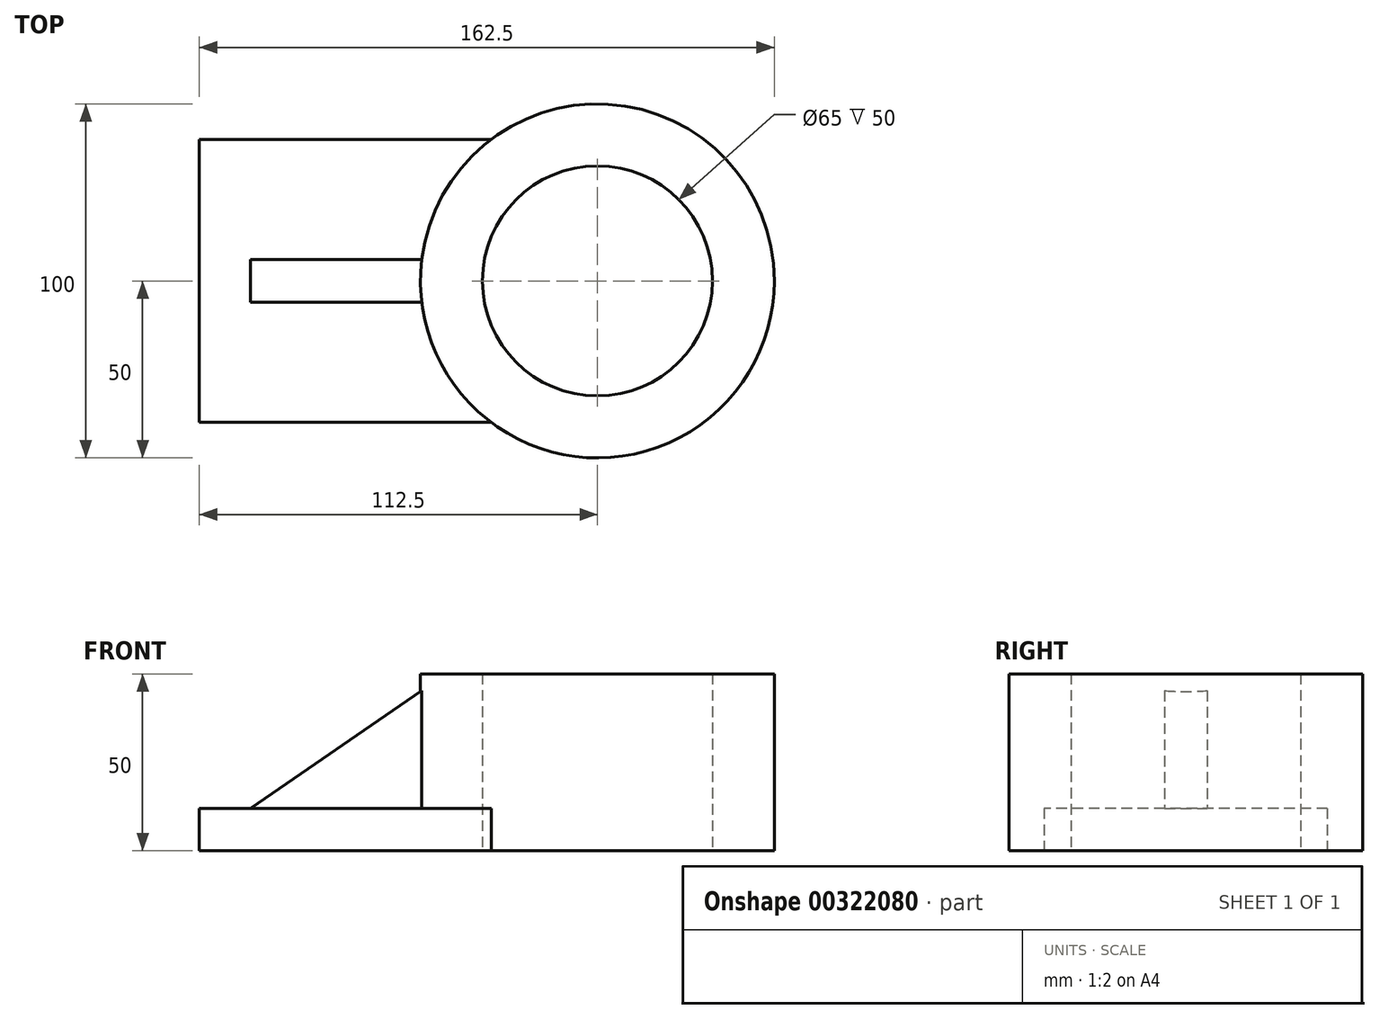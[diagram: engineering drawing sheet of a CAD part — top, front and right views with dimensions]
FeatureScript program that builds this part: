
annotation { "Feature Type Name" : "Feature", "Feature Type Description" : "" }
export const myFeature = defineFeature(function(context is Context, id is Id, definition is map)
    precondition{}
    {
        {
            var Q0;
            Q0=qCreatedBy(makeId("Top.planeOp"),FACE);
            var sketch = newSketch(context, id + "F0", { "sketchPlane" : qUnion([Q0])});
            skLineSegment(sketch, "E0.bottom", {"start": v(-80, 40) * mm, "end": v(2.5, 40) * mm});
            skLineSegment(sketch, "E0.top", {"start": v(-80, -40) * mm, "end": v(2.5, -40) * mm});
            skLineSegment(sketch, "E0.left", {"start": v(-80, 40) * mm, "end": v(-80, -40) * mm});
            skPoint(sketch, "E0.middle", {"position": v(-38.75, 0) * mm});
            skCircle(sketch, "E1", {"center": v(32.5, 0) * mm, "radius": 50 * mm});
            skPoint(sketch, "E1.second.point", {"position": v(82.5, 0) * mm});
            skCircle(sketch, "E2", {"center": v(32.5, 0) * mm, "radius": 32.5 * mm});
            skSolve(sketch);
        }
        {
            var Q0;
            Q0=makeQuery(id+"F0.imprint","IMPRINT",FACE,{"disambiguationData":[TD([[makeQuery(id+"F0.imprint","IMPRINT",EDGE,{"derivedFrom":sQuery(id+"F0.wireOp",EDGE,"E2")}),-1.0]])]});
            extrude(context, id + "F1", {"entities" : qUnion([Q0]), "depth" : 50 * mm});
        }
        {
            var Q0;
            Q0 = qSketchRegion(id + "F0", true);
            extrude(context, id + "F2", {"entities" : qUnion([Q0]), "operationType" : NewBodyOperationType.ADD, "depth" : 12 * mm});
        }
        {
            var Q0;
            Q0=qCreatedBy(makeId("Front.planeOp"),FACE);
            var sketch = newSketch(context, id + "F3", { "sketchPlane" : qUnion([Q0])});
            skLineSegment(sketch, "E3", {"start": v(-67.73, 10.5) * mm, "end": v(-15.42, 46.42) * mm});
            skLineSegment(sketch, "E4", {"start": v(-15.42, 46.42) * mm, "end": v(-15.42, 10.5) * mm});
            skLineSegment(sketch, "E5", {"start": v(-67.73, 10.5) * mm, "end": v(-15.42, 10.5) * mm});
            skSolve(sketch);
        }
        {
            var Q0;
            Q0 = qSketchRegion(id + "F3", true);
            extrude(context, id + "F4", {"entities" : qUnion([Q0]), "operationType" : NewBodyOperationType.ADD, "oppositeDirection" : true, "depth" : 6 * mm, "hasSecondDirection" : true, "secondDirectionOppositeDirection" : false, "secondDirectionDepth" : 6 * mm});
        }
    });
